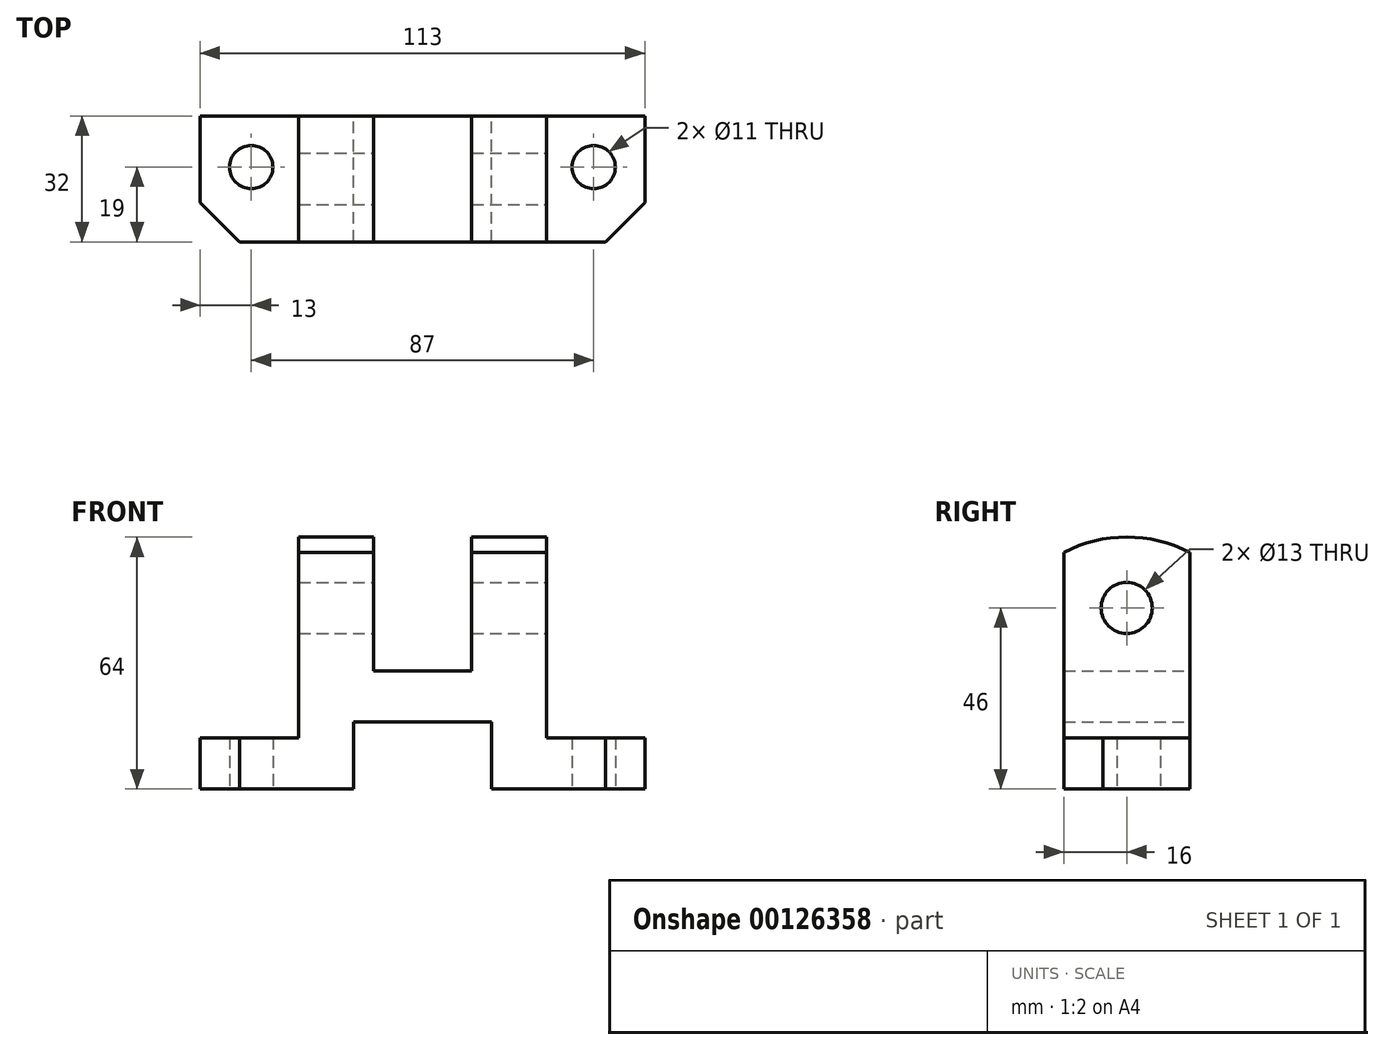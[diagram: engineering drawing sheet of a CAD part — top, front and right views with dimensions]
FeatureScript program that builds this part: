
annotation { "Feature Type Name" : "Feature", "Feature Type Description" : "" }
export const myFeature = defineFeature(function(context is Context, id is Id, definition is map)
    precondition{}
    {
        {
            var Q0;
            Q0=qCreatedBy(makeId("Front.planeOp"),FACE);
            var sketch = newSketch(context, id + "F0", { "sketchPlane" : qUnion([Q0])});
            skLineSegment(sketch, "E0", {"start": v(0, 0) * mm, "end": v(39, 0) * mm});
            skLineSegment(sketch, "E1", {"start": v(39, 0) * mm, "end": v(39, 17) * mm});
            skLineSegment(sketch, "E2", {"start": v(39, 17) * mm, "end": v(74, 17) * mm});
            skLineSegment(sketch, "E3", {"start": v(74, 17) * mm, "end": v(74, 0) * mm});
            skLineSegment(sketch, "E4", {"start": v(74, 0) * mm, "end": v(113, 0) * mm});
            skLineSegment(sketch, "E5", {"start": v(113, 0) * mm, "end": v(113, 13) * mm});
            skLineSegment(sketch, "E6", {"start": v(113, 13) * mm, "end": v(88, 13) * mm});
            skLineSegment(sketch, "E7", {"start": v(88, 13) * mm, "end": v(88, 64) * mm});
            skLineSegment(sketch, "E8", {"start": v(88, 64) * mm, "end": v(69, 64) * mm});
            skLineSegment(sketch, "E9", {"start": v(69, 64) * mm, "end": v(69, 30) * mm});
            skLineSegment(sketch, "E10", {"start": v(69, 30) * mm, "end": v(44, 30) * mm});
            skLineSegment(sketch, "E11", {"start": v(44, 30) * mm, "end": v(44, 64) * mm});
            skLineSegment(sketch, "E12", {"start": v(44, 64) * mm, "end": v(25, 64) * mm});
            skLineSegment(sketch, "E13", {"start": v(25, 64) * mm, "end": v(25, 13) * mm});
            skLineSegment(sketch, "E14", {"start": v(25, 13) * mm, "end": v(0, 13) * mm});
            skLineSegment(sketch, "E15", {"start": v(0, 13) * mm, "end": v(0, 0) * mm});
            skSolve(sketch);
        }
        {
            var Q0;
            Q0=makeQuery(id+"F0.imprint","IMPRINT",FACE,{"disambiguationData":[TD([[makeQuery(id+"F0.imprint","IMPRINT",EDGE,{"derivedFrom":sQuery(id+"F0.wireOp",EDGE,"E0")}),1.0]])]});
            extrude(context, id + "F1", {"entities" : qUnion([Q0]), "endBound" : BoundingType.SYMMETRIC, "depth" : 32 * mm});
        }
        {
            var Q0;
            Q0=makeQuery(id+"F1.opExtrude","SWEPT_FACE",FACE,{"disambiguationData":[OSD([sQuery(id+"F0.wireOp",EDGE,"E7")])]});
            var sketch = newSketch(context, id + "F2", { "sketchPlane" : qUnion([Q0])});
            skLineSegment(sketch, "E16", {"start": v(0, 13) * mm, "end": v(0, 46) * mm, "construction": true});
            skPoint(sketch, "E16.endSnap0", {"position": v(0, 64) * mm});
            skCircle(sketch, "E17", {"center": v(0, 46) * mm, "radius": 6.5 * mm});
            skSolve(sketch);
        }
        {
            var Q0;
            Q0=makeQuery(id+"F2.imprint","IMPRINT",FACE,{"disambiguationData":[TD([[makeQuery(id+"F2.imprint","IMPRINT",EDGE,{"derivedFrom":sQuery(id+"F2.wireOp",EDGE,"E17")}),1.0]])]});
            extrude(context, id + "F3", {"entities" : qUnion([Q0]), "operationType" : NewBodyOperationType.REMOVE, "oppositeDirection" : true, "depth" : 80 * mm});
        }
        {
            var Q0;
            Q0=makeQuery(id+"F1.opExtrude","SWEPT_FACE",FACE,{"disambiguationData":[OSD([sQuery(id+"F0.wireOp",EDGE,"E7")])]});
            var sketch = newSketch(context, id + "F4", { "sketchPlane" : qUnion([Q0])});
            skPoint(sketch, "E18.endSnap0", {"position": v(0, 64) * mm});
            skLineSegment(sketch, "E19", {"start": v(0, 64) * mm, "end": v(0, 29) * mm, "construction": true});
            skArc(sketch, "E20", {"start": v(-16, 60.13) * mm, "mid": v(0, 64) * mm, "end": v(16, 60.13) * mm});
            skLineSegment(sketch, "E21", {"start": v(-16, 60.13) * mm, "end": v(-16, 64) * mm});
            skLineSegment(sketch, "E22", {"start": v(-16, 64) * mm, "end": v(16, 64) * mm});
            skLineSegment(sketch, "E23", {"start": v(16, 64) * mm, "end": v(16, 60.13) * mm});
            skSolve(sketch);
        }
        {
            var Q0;
            {var subQ0=sQuery(id+"F4.wireOp",EDGE,"E21");Q0=makeQuery(id+"F4.imprint","IMPRINT",FACE,{"disambiguationData":[TD([[makeQuery(id+"F4.imprint","IMPRINT",EDGE,{"derivedFrom":subQ0}),-1.0]])]});}
            var Q1;
            {var subQ0=sQuery(id+"F4.wireOp",EDGE,"E23");Q1=makeQuery(id+"F4.imprint","IMPRINT",FACE,{"disambiguationData":[TD([[makeQuery(id+"F4.imprint","IMPRINT",EDGE,{"derivedFrom":subQ0}),1.0]])]});}
            extrude(context, id + "F5", {"entities" : qUnion([Q0, Q1]), "operationType" : NewBodyOperationType.REMOVE, "oppositeDirection" : true, "depth" : 80 * mm});
        }
        {
            var Q0;
            Q0=makeQuery(id+"F1.opExtrude","SWEPT_FACE",FACE,{"disambiguationData":[OSD([sQuery(id+"F0.wireOp",EDGE,"E0")])]});
            var sketch = newSketch(context, id + "F6", { "sketchPlane" : qUnion([Q0])});
            skLineSegment(sketch, "E24", {"start": v(0, 16) * mm, "end": v(0, 6) * mm});
            skLineSegment(sketch, "E25", {"start": v(0, 16) * mm, "end": v(10, 16) * mm});
            skLineSegment(sketch, "E26", {"start": v(10, 16) * mm, "end": v(0, 6) * mm});
            skLineSegment(sketch, "E27", {"start": v(113, 16) * mm, "end": v(103, 16) * mm});
            skLineSegment(sketch, "E28", {"start": v(113, 16) * mm, "end": v(113, 6) * mm});
            skLineSegment(sketch, "E29", {"start": v(113, 6) * mm, "end": v(103, 16) * mm});
            skLineSegment(sketch, "E30", {"start": v(0, 0) * mm, "end": v(13, 0) * mm, "construction": true});
            skLineSegment(sketch, "E31", {"start": v(13, 0) * mm, "end": v(100, 0) * mm, "construction": true});
            skLineSegment(sketch, "E32", {"start": v(13, 0) * mm, "end": v(13, -3) * mm, "construction": true});
            skLineSegment(sketch, "E33", {"start": v(100, 0) * mm, "end": v(100, -3) * mm, "construction": true});
            skCircle(sketch, "E34", {"center": v(13, -3) * mm, "radius": 5.5 * mm});
            skCircle(sketch, "E35", {"center": v(100, -3) * mm, "radius": 5.5 * mm});
            skSolve(sketch);
        }
        {
            var Q0;
            Q0=makeQuery(id+"F6.imprint","IMPRINT",FACE,{"disambiguationData":[TD([[makeQuery(id+"F6.imprint","IMPRINT",EDGE,{"derivedFrom":sQuery(id+"F6.wireOp",EDGE,"E24")}),1.0]])]});
            var Q1;
            Q1=makeQuery(id+"F6.imprint","IMPRINT",FACE,{"disambiguationData":[TD([[makeQuery(id+"F6.imprint","IMPRINT",EDGE,{"derivedFrom":sQuery(id+"F6.wireOp",EDGE,"E34")}),1.0]])]});
            var Q2;
            Q2=makeQuery(id+"F6.imprint","IMPRINT",FACE,{"disambiguationData":[TD([[makeQuery(id+"F6.imprint","IMPRINT",EDGE,{"derivedFrom":sQuery(id+"F6.wireOp",EDGE,"E35")}),1.0]])]});
            var Q3;
            Q3=makeQuery(id+"F6.imprint","IMPRINT",FACE,{"disambiguationData":[TD([[makeQuery(id+"F6.imprint","IMPRINT",EDGE,{"derivedFrom":sQuery(id+"F6.wireOp",EDGE,"E27")}),1.0]])]});
            extrude(context, id + "F7", {"entities" : qUnion([Q0, Q1, Q2, Q3]), "operationType" : NewBodyOperationType.REMOVE, "oppositeDirection" : true, "depth" : 25 * mm});
        }
    });
